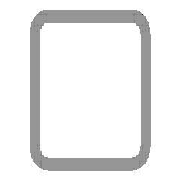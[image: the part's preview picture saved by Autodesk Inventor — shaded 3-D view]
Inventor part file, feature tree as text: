
AUTODESK INVENTOR PART (.ipt)
format: ipt  version: 2022 (Build 260153000, 153)  size: 638,976 bytes
history: native  units: mm (DEFAULTED — no unit token found)
features: other x8, sketch x3, plane x2, surface_op x2, split x1
ambient origin geometry x8: Origin, YZ Plane, XZ Plane, XY Plane, X Axis, Y Axis, Z Axis, Center Point
bodies: Solid1 (feature_tree), Body (feature_tree), Solid5 (feature_tree), Solid6 (feature_tree)
feature tree (16):
  parser-record x1  (decoder bookkeeping rows leaked as tree rows — omitted from the tree; the rows remain in map.json)
  other  "Driven Length"
  other  "Start Plane"
  other  "End Plane"
  plane  "Work Plane4"
  split  "Split1"
  sketch  "Sketch"  dims[d7=4.0mm d9=40.0mm d11=40.0mm d12=2.0mm d13=20.0mm d14=300.0mm d15=20.0mm d16=20.0mm d17=90.0deg d18=280.0mm d55=5.0mm d56=5.0mm d57=5.0mm d58=5.0mm d59=5.0mm d60=5.0mm d61=5.0mm d62=5.0mm d63=0.0mm d64=5.0mm d65=5.0mm d66=5.0mm d67=5.0mm d68=5.0mm d69=5.0mm d70=5.0mm d71=5.0mm d72=0.0mm]
  sketch  "Sketch3"  dims[d3=280.0mm]
  plane  "Work Plane3"
  sketch  "Sketch4"  dims[d4=0.0mm]
  other  "Srf9"
  other  "Srf10"
  other  "Srf8"
  surface_op  "Boundary Patch5"
  surface_op  "Boundary Patch6"
  other  "Srf11"
